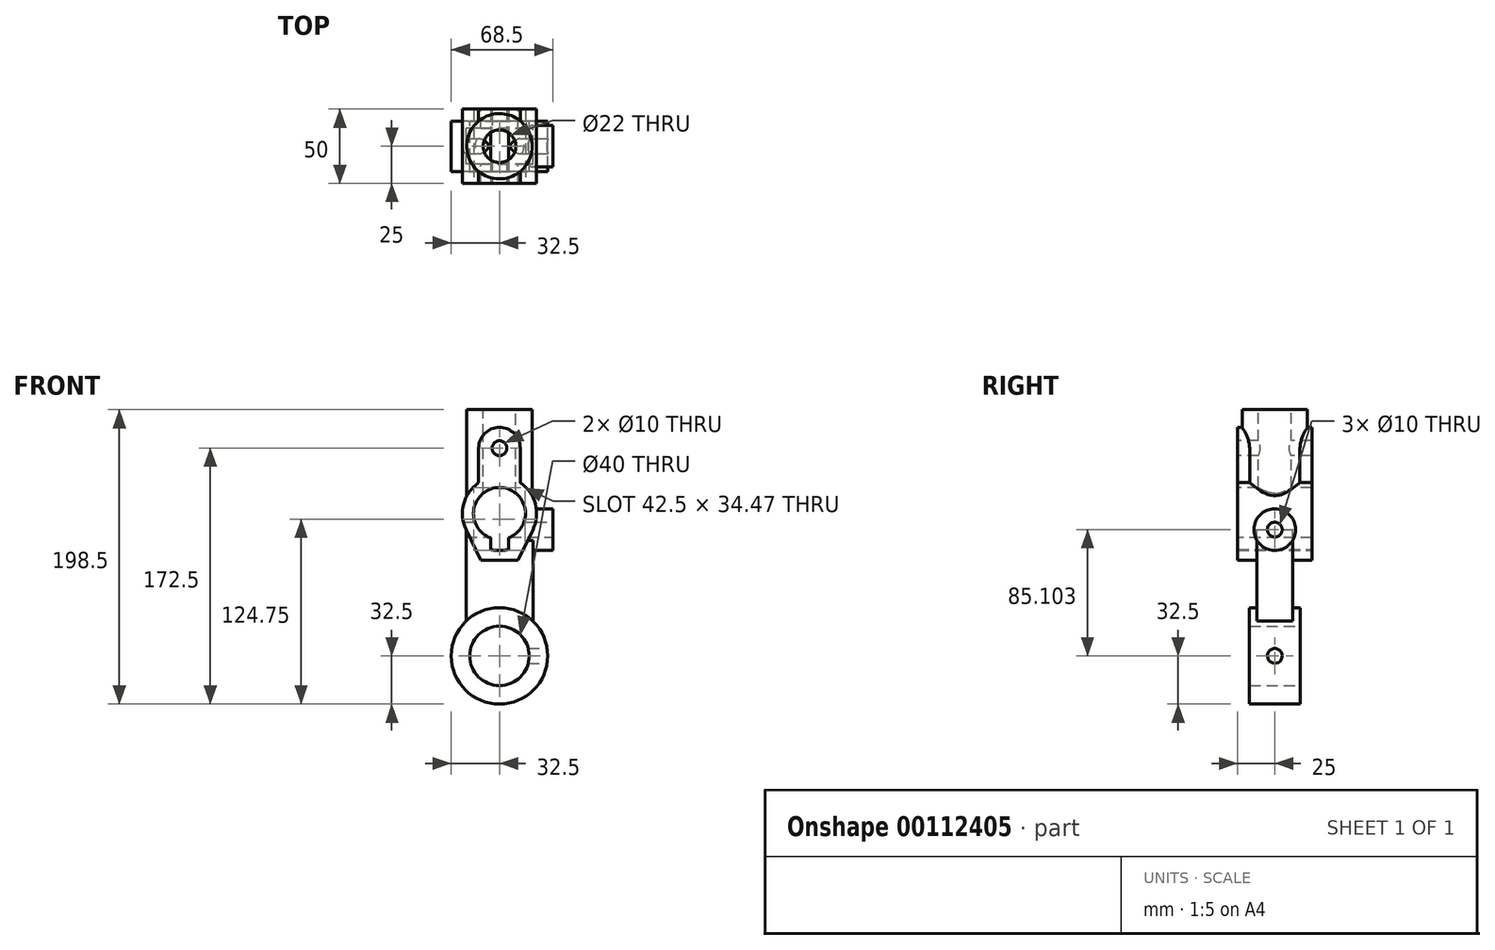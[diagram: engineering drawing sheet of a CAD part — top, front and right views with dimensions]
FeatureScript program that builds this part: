
annotation { "Feature Type Name" : "Feature", "Feature Type Description" : "" }
export const myFeature = defineFeature(function(context is Context, id is Id, definition is map)
    precondition{}
    {
        {
            var Q0;
            Q0=qCreatedBy(makeId("Front.planeOp"),FACE);
            var sketch = newSketch(context, id + "F0", { "sketchPlane" : qUnion([Q0])});
            skLineSegment(sketch, "E0", {"start": v(-47.55, 0) * mm, "end": v(54.1, 0) * mm, "construction": true});
            skLineSegment(sketch, "E1", {"start": v(0, -44.28) * mm, "end": v(0, 46.07) * mm, "construction": true});
            skLineSegment(sketch, "E2", {"start": v(-29.72, 96) * mm, "end": v(30.91, 96) * mm, "construction": true});
            skLineSegment(sketch, "E3", {"start": v(0, 110.32) * mm, "end": v(0, 80.07) * mm, "construction": true});
            skLineSegment(sketch, "E4", {"start": v(0, 152.21) * mm, "end": v(0, 123.62) * mm, "construction": true});
            skLineSegment(sketch, "E5", {"start": v(-23.78, 140) * mm, "end": v(32.25, 140) * mm, "construction": true});
            skSolve(sketch);
        }
        {
            var Q0;
            Q0=qCreatedBy(makeId("Front.planeOp"),FACE);
            var sketch = newSketch(context, id + "F1", { "sketchPlane" : qUnion([Q0])});
            skCircle(sketch, "E6", {"center": v(0, 0) * mm, "radius": 32.5 * mm});
            skLineSegment(sketch, "E7", {"start": v(-22.5, 23.45) * mm, "end": v(-22.5, 96) * mm});
            skLineSegment(sketch, "E8", {"start": v(-22.5, 96) * mm, "end": v(22.5, 96) * mm});
            skLineSegment(sketch, "E9", {"start": v(22.5, 96) * mm, "end": v(22.5, 23.45) * mm});
            skCircle(sketch, "E10", {"center": v(0, 0) * mm, "radius": 20 * mm});
            skCircle(sketch, "E11", {"center": v(0, 140) * mm, "radius": 5 * mm});
            skArc(sketch, "E12", {"start": v(6, 79.56) * mm, "mid": v(0, 113.5) * mm, "end": v(-6, 79.56) * mm});
            skLineSegment(sketch, "E13.bottom", {"start": v(6, 79.56) * mm, "end": v(6, 79.56) * mm});
            skLineSegment(sketch, "E13.top", {"start": v(-6, 73.6) * mm, "end": v(6, 73.6) * mm});
            skLineSegment(sketch, "E13.left", {"start": v(-6, 79.56) * mm, "end": v(-6, 73.6) * mm});
            skLineSegment(sketch, "E13.right", {"start": v(6, 79.56) * mm, "end": v(6, 73.6) * mm});
            skLineSegment(sketch, "E14", {"start": v(-12.5, 64.46) * mm, "end": v(12.5, 64.46) * mm});
            skLineSegment(sketch, "E15", {"start": v(12.5, 64.46) * mm, "end": v(22.5, 85.1) * mm});
            skLineSegment(sketch, "E16", {"start": v(-12.5, 64.46) * mm, "end": v(-22.5, 85.1) * mm});
            skArc(sketch, "E17", {"start": v(-14, 116.71) * mm, "mid": v(-24.14, 102.5) * mm, "end": v(-22.5, 85.1) * mm});
            skArc(sketch, "E18", {"start": v(22.5, 85.1) * mm, "mid": v(24.14, 102.5) * mm, "end": v(14, 116.71) * mm});
            skLineSegment(sketch, "E19", {"start": v(14, 116.71) * mm, "end": v(14, 140) * mm});
            skArc(sketch, "E20", {"start": v(14, 140) * mm, "mid": v(0, 154) * mm, "end": v(-14, 140) * mm});
            skLineSegment(sketch, "E21", {"start": v(-14, 140) * mm, "end": v(-14, 116.71) * mm});
            skSolve(sketch);
        }
        {
            var Q0;
            Q0=qCreatedBy(makeId("Top.planeOp"),FACE);
            cPlane(context, id + "F2", {"entities" : qUnion([Q0]), "cplaneType" : CPlaneType.OFFSET, "offset" : 96 * mm, "width" : 150 * mm, "height" : 150 * mm});
        }
        {
            var Q0;
            Q0=makeQuery(id+"F1.imprint","IMPRINT",FACE,{"disambiguationData":[TD([[makeQuery(id+"F1.imprint","IMPRINT",EDGE,{"derivedFrom":sQuery(id+"F1.wireOp",EDGE,"E14")}),-1.0]])]});
            extrude(context, id + "F3", {"entities" : qUnion([Q0]), "endBound" : BoundingType.SYMMETRIC, "depth" : 24 * mm});
        }
        {
            var Q0;
            Q0=qCreatedBy(id+"F2.planeOp",FACE);
            var sketch = newSketch(context, id + "F4", { "sketchPlane" : qUnion([Q0])});
            skCircle(sketch, "E22", {"center": v(0, 0) * mm, "radius": 11 * mm});
            skCircle(sketch, "E23", {"center": v(0, 0) * mm, "radius": 22 * mm});
            skSolve(sketch);
        }
        {
            var Q0;
            Q0=makeQuery(id+"F1.imprint","IMPRINT",FACE,{"disambiguationData":[TD([[makeQuery(id+"F1.imprint","IMPRINT",EDGE,{"derivedFrom":sQuery(id+"F1.wireOp",EDGE,"E10")}),-1.0]])]});
            extrude(context, id + "F5", {"entities" : qUnion([Q0]), "operationType" : NewBodyOperationType.ADD, "endBound" : BoundingType.SYMMETRIC, "depth" : 34 * mm});
        }
        {
            var Q0;
            Q0=makeQuery(id+"F1.imprint","IMPRINT",FACE,{"disambiguationData":[TD([[makeQuery(id+"F1.imprint","IMPRINT",EDGE,{"derivedFrom":sQuery(id+"F1.wireOp",EDGE,"E11")}),-1.0]])]});
            var Q1;
            Q1=makeQuery(id+"F1.imprint","IMPRINT",FACE,{"disambiguationData":[TD([[makeQuery(id+"F1.imprint","IMPRINT",EDGE,{"derivedFrom":sQuery(id+"F1.wireOp",EDGE,"E13.top")}),-1.0]])]});
            var Q2;
            {var subQ0=sQuery(id+"F1.wireOp",EDGE,"E12");var subQ1=sQuery(id+"F1.wireOp",EDGE,"E8");var subQ2=makeQuery(id+"F1.imprint","INTERSECT",VERTEX,{"disambiguationData":[OD(0.0)],"derivedFrom":[subQ1,subQ0]});Q2=makeQuery(id+"F1.imprint","IMPRINT",FACE,{"disambiguationData":[TD([[makeQuery(id+"F1.imprint","IMPRINT",EDGE,{"disambiguationData":[TD([[subQ2,-1.0]])],"derivedFrom":subQ1}),1.0]])]});}
            var Q3;
            Q3=makeQuery(id+"F1.imprint","IMPRINT",FACE,{"disambiguationData":[TD([[makeQuery(id+"F1.imprint","IMPRINT",EDGE,{"derivedFrom":sQuery(id+"F1.wireOp",EDGE,"E13.top")}),1.0]])]});
            var Q4;
            Q4=makeQuery(id+"F1.imprint","IMPRINT",FACE,{"disambiguationData":[TD([[makeQuery(id+"F1.imprint","IMPRINT",EDGE,{"derivedFrom":sQuery(id+"F1.wireOp",EDGE,"E11")}),1.0]])]});
            extrude(context, id + "F6", {"entities" : qUnion([Q0, Q1, Q2, Q3, Q4]), "operationType" : NewBodyOperationType.ADD, "endBound" : BoundingType.SYMMETRIC, "depth" : 50 * mm});
        }
        {
            var Q0;
            Q0=makeQuery(id+"F6.opExtrude","CAP_FACE",FACE,{"disambiguationData":[OSD([sQuery(id+"F1.wireOp",EDGE,"E14"),sQuery(id+"F1.wireOp",EDGE,"E15"),sQuery(id+"F1.wireOp",EDGE,"E16"),sQuery(id+"F1.wireOp",EDGE,"E17"),sQuery(id+"F1.wireOp",EDGE,"E18"),sQuery(id+"F1.wireOp",EDGE,"E19"),sQuery(id+"F1.wireOp",EDGE,"E20"),sQuery(id+"F1.wireOp",EDGE,"E21")])],"isStart":false});
            var sketch = newSketch(context, id + "F7", { "sketchPlane" : qUnion([Q0])});
            skCircle(sketch, "E24.0", {"center": v(0, 140) * mm, "radius": 5 * mm});
            skArc(sketch, "E25.0", {"start": v(6, 79.56) * mm, "mid": v(0, 113.5) * mm, "end": v(-6, 79.56) * mm});
            skLineSegment(sketch, "E26.0", {"start": v(-6, 73.6) * mm, "end": v(6, 73.6) * mm});
            skLineSegment(sketch, "E26.1", {"start": v(-6, 79.56) * mm, "end": v(-6, 73.6) * mm});
            skLineSegment(sketch, "E26.2", {"start": v(6, 79.56) * mm, "end": v(6, 73.6) * mm});
            skSolve(sketch);
        }
        {
            var Q0;
            Q0=qCreatedBy(makeId("Right.planeOp"),FACE);
            cPlane(context, id + "F8", {"entities" : qUnion([Q0]), "cplaneType" : CPlaneType.OFFSET, "offset" : 36 * mm, "width" : 150 * mm, "height" : 150 * mm});
        }
        {
            var Q0;
            Q0=makeQuery(id+"F4.imprint","IMPRINT",FACE,{"disambiguationData":[TD([[makeQuery(id+"F4.imprint","IMPRINT",EDGE,{"derivedFrom":sQuery(id+"F4.wireOp",EDGE,"E22")}),1.0]])]});
            var Q1;
            Q1=makeQuery(id+"F4.imprint","IMPRINT",FACE,{"disambiguationData":[TD([[makeQuery(id+"F4.imprint","IMPRINT",EDGE,{"derivedFrom":sQuery(id+"F4.wireOp",EDGE,"E22")}),-1.0]])]});
            var Q2;
            Q2=sQuery(id+"F4.wireOp",EDGE,"E22");
            var Q3;
            Q3=sQuery(id+"F4.wireOp",EDGE,"E23");
            extrude(context, id + "F9", {"entities" : qUnion([Q0, Q1]), "operationType" : NewBodyOperationType.ADD, "surfaceEntities" : qUnion([Q2, Q3]), "depth" : 70 * mm});
        }
        {
            var Q0;
            Q0=qCreatedBy(id+"F8.planeOp",FACE);
            var sketch = newSketch(context, id + "F10", { "sketchPlane" : qUnion([Q0])});
            skCircle(sketch, "E27", {"center": v(0, 85.1) * mm, "radius": 14 * mm});
            skSolve(sketch);
        }
        {
            var Q0;
            Q0 = qSketchRegion(id + "F10", true);
            extrude(context, id + "F11", {"entities" : qUnion([Q0]), "operationType" : NewBodyOperationType.ADD, "endBound" : BoundingType.UP_TO_NEXT, "oppositeDirection" : true, "depth" : 25 * mm});
        }
        {
            var Q0;
            Q0=makeQuery(id+"F9.opExtrude","CAP_FACE",FACE,{"disambiguationData":[OSD([sQuery(id+"F4.wireOp",EDGE,"E23")])],"isStart":false});
            var sketch = newSketch(context, id + "F12", { "sketchPlane" : qUnion([Q0])});
            skCircle(sketch, "E28.0", {"center": v(0, 0) * mm, "radius": 11 * mm});
            skSolve(sketch);
        }
        {
            var Q0;
            Q0=qCreatedBy(id+"F8.planeOp",FACE);
            var sketch = newSketch(context, id + "F13", { "sketchPlane" : qUnion([Q0])});
            skCircle(sketch, "E29", {"center": v(0, 85.1) * mm, "radius": 5 * mm});
            skSolve(sketch);
        }
        {
            var Q0;
            Q0 = qSketchRegion(id + "F13", true);
            extrude(context, id + "F14", {"entities" : qUnion([Q0]), "operationType" : NewBodyOperationType.REMOVE, "endBound" : BoundingType.UP_TO_NEXT, "oppositeDirection" : true, "depth" : 25 * mm});
        }
        {
            var Q0;
            Q0=makeQuery(id+"F7.imprint","IMPRINT",FACE,{"disambiguationData":[TD([[makeQuery(id+"F7.imprint","IMPRINT",EDGE,{"derivedFrom":sQuery(id+"F7.wireOp",EDGE,"E24.0")}),1.0]])]});
            var Q1;
            Q1=makeQuery(id+"F7.imprint","IMPRINT",FACE,{"disambiguationData":[TD([[makeQuery(id+"F7.imprint","IMPRINT",EDGE,{"derivedFrom":sQuery(id+"F7.wireOp",EDGE,"E25.0")}),1.0]])]});
            extrude(context, id + "F15", {"entities" : qUnion([Q0, Q1]), "operationType" : NewBodyOperationType.REMOVE, "endBound" : BoundingType.THROUGH_ALL, "oppositeDirection" : true, "depth" : 25 * mm});
        }
        {
            var Q0;
            Q0=makeQuery(id+"F12.imprint","IMPRINT",FACE,{"disambiguationData":[TD([[makeQuery(id+"F12.imprint","IMPRINT",EDGE,{"derivedFrom":sQuery(id+"F12.wireOp",EDGE,"E28.0")}),1.0]])]});
            var Q1;
            Q1=makeQuery(id+"F15.boolean.opBoolean","COPY",FACE,{"derivedFrom":makeQuery(id+"F15.opExtrude","SWEPT_FACE",FACE,{"disambiguationData":[OSD([sQuery(id+"F7.wireOp",EDGE,"E26.0")])]})});
            var Q2;
            Q2=sQuery(id+"F12.wireOp",EDGE,"E28.0");
            var Q3;
            Q3=makeQuery(id+"F6.opExtrude","SWEPT_FACE",FACE,{"disambiguationData":[OSD([sQuery(id+"F1.wireOp",EDGE,"E18")])]});
            extrude(context, id + "F16", {"entities" : qUnion([Q0, Q1]), "operationType" : NewBodyOperationType.REMOVE, "surfaceEntities" : qUnion([Q2]), "endBound" : BoundingType.UP_TO_SURFACE, "oppositeDirection" : true, "endBoundEntityFace" : qUnion([Q3]), "depth" : 25 * mm});
        }
        {
            var Q0;
            Q0=qCreatedBy(id+"F8.planeOp",FACE);
            var sketch = newSketch(context, id + "F17", { "sketchPlane" : qUnion([Q0])});
            skCircle(sketch, "E30", {"center": v(0, 0) * mm, "radius": 5 * mm});
            skSolve(sketch);
        }
        {
            var Q0;
            Q0 = qSketchRegion(id + "F17", true);
            extrude(context, id + "F18", {"entities" : qUnion([Q0]), "operationType" : NewBodyOperationType.REMOVE, "oppositeDirection" : true, "depth" : 25 * mm});
        }
        {
            var Q0;
            Q0=makeQuery(id+"F4.imprint","IMPRINT",FACE,{"disambiguationData":[TD([[makeQuery(id+"F4.imprint","IMPRINT",EDGE,{"derivedFrom":sQuery(id+"F4.wireOp",EDGE,"E22")}),1.0]])]});
            extrude(context, id + "F19", {"entities" : qUnion([Q0]), "operationType" : NewBodyOperationType.REMOVE, "endBound" : BoundingType.THROUGH_ALL, "depth" : 25 * mm});
        }
    });
